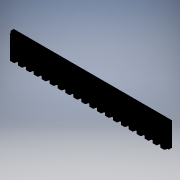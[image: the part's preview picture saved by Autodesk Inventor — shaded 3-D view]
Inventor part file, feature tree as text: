
AUTODESK INVENTOR PART (.ipt)
format: ipt  version: 2017.3 (Build 213256000, 256)  size: 261,120 bytes
history: native  units: mm (DEFAULTED — no unit token found)
features: extrude x1, sketch x1
ambient origin geometry x8: Origin, YZ Plane, XZ Plane, XY Plane, X Axis, Y Axis, Z Axis, Center Point
bodies: Solid1 (feature_tree)
feature tree (2):
  extrude  "Extrusion1"  [1 undecoded]
  sketch  "Sketch_1"  dims[d0=15.0mm d1=0.0mm]
note: 1 required parameter value undecoded (feature->parameter linkage not recoverable at this tier; creation-order binding heuristic only, values carry confidence <= 0.55)
